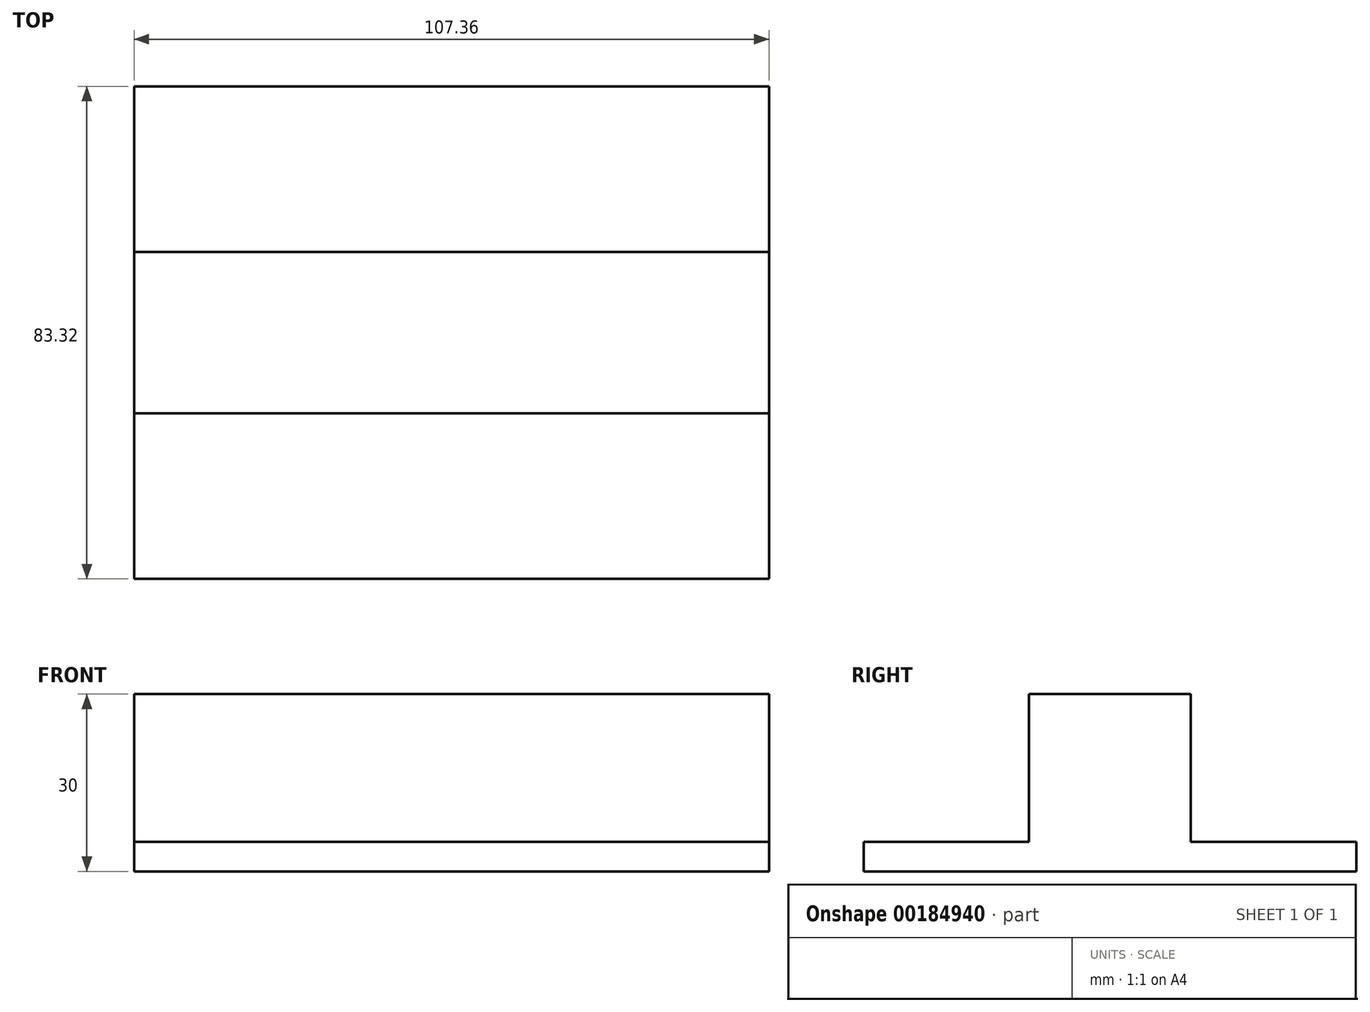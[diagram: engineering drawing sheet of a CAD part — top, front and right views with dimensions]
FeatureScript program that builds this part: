
annotation { "Feature Type Name" : "Feature", "Feature Type Description" : "" }
export const myFeature = defineFeature(function(context is Context, id is Id, definition is map)
    precondition{}
    {
        {
            var Q0;
            Q0=qCreatedBy(makeId("Top.planeOp"),FACE);
            var sketch = newSketch(context, id + "F0", { "sketchPlane" : qUnion([Q0])});
            skLineSegment(sketch, "E0.bottom", {"start": v(53.68, -41.66) * mm, "end": v(-53.68, -41.66) * mm});
            skLineSegment(sketch, "E0.top", {"start": v(53.68, 41.66) * mm, "end": v(-53.68, 41.66) * mm});
            skLineSegment(sketch, "E0.left", {"start": v(53.68, -41.66) * mm, "end": v(53.68, 41.66) * mm});
            skLineSegment(sketch, "E0.right", {"start": v(-53.68, -41.66) * mm, "end": v(-53.68, 41.66) * mm});
            skPoint(sketch, "E0.middle", {"position": v(0, 0) * mm});
            skSolve(sketch);
        }
        {
            var Q0;
            Q0=makeQuery(id+"F0.imprint","IMPRINT",FACE,{"disambiguationData":[TD([[makeQuery(id+"F0.imprint","IMPRINT",EDGE,{"derivedFrom":sQuery(id+"F0.wireOp",EDGE,"E0.bottom")}),-1.0]])]});
            extrude(context, id + "F2", {"entities" : qUnion([Q0]), "depth" : 5 * mm});
        }
        {
            var Q0;
            Q0=makeQuery(id+"F2.opExtrude","CAP_FACE",FACE,{"disambiguationData":[OSD([sQuery(id+"F0.wireOp",EDGE,"E0.bottom"),sQuery(id+"F0.wireOp",EDGE,"E0.top"),sQuery(id+"F0.wireOp",EDGE,"E0.left"),sQuery(id+"F0.wireOp",EDGE,"E0.right")])],"isStart":false});
            var sketch = newSketch(context, id + "F1", { "sketchPlane" : qUnion([Q0])});
            skLineSegment(sketch, "E1.bottom", {"start": v(53.68, 13.66) * mm, "end": v(-53.68, 13.66) * mm});
            skLineSegment(sketch, "E1.top", {"start": v(53.68, -13.66) * mm, "end": v(-53.68, -13.66) * mm});
            skLineSegment(sketch, "E1.left", {"start": v(53.68, 13.66) * mm, "end": v(53.68, -13.66) * mm});
            skLineSegment(sketch, "E1.right", {"start": v(-53.68, 13.66) * mm, "end": v(-53.68, -13.66) * mm});
            skPoint(sketch, "E1.middle", {"position": v(0, 0) * mm});
            skSolve(sketch);
        }
        {
            var Q0;
            Q0=makeQuery(id+"F1.imprint","IMPRINT",FACE,{"disambiguationData":[TD([[makeQuery(id+"F1.imprint","IMPRINT",EDGE,{"derivedFrom":sQuery(id+"F1.wireOp",EDGE,"E1.bottom")}),1.0]])]});
            extrude(context, id + "F3", {"entities" : qUnion([Q0]), "operationType" : NewBodyOperationType.ADD, "depth" : 25 * mm});
        }
    });
